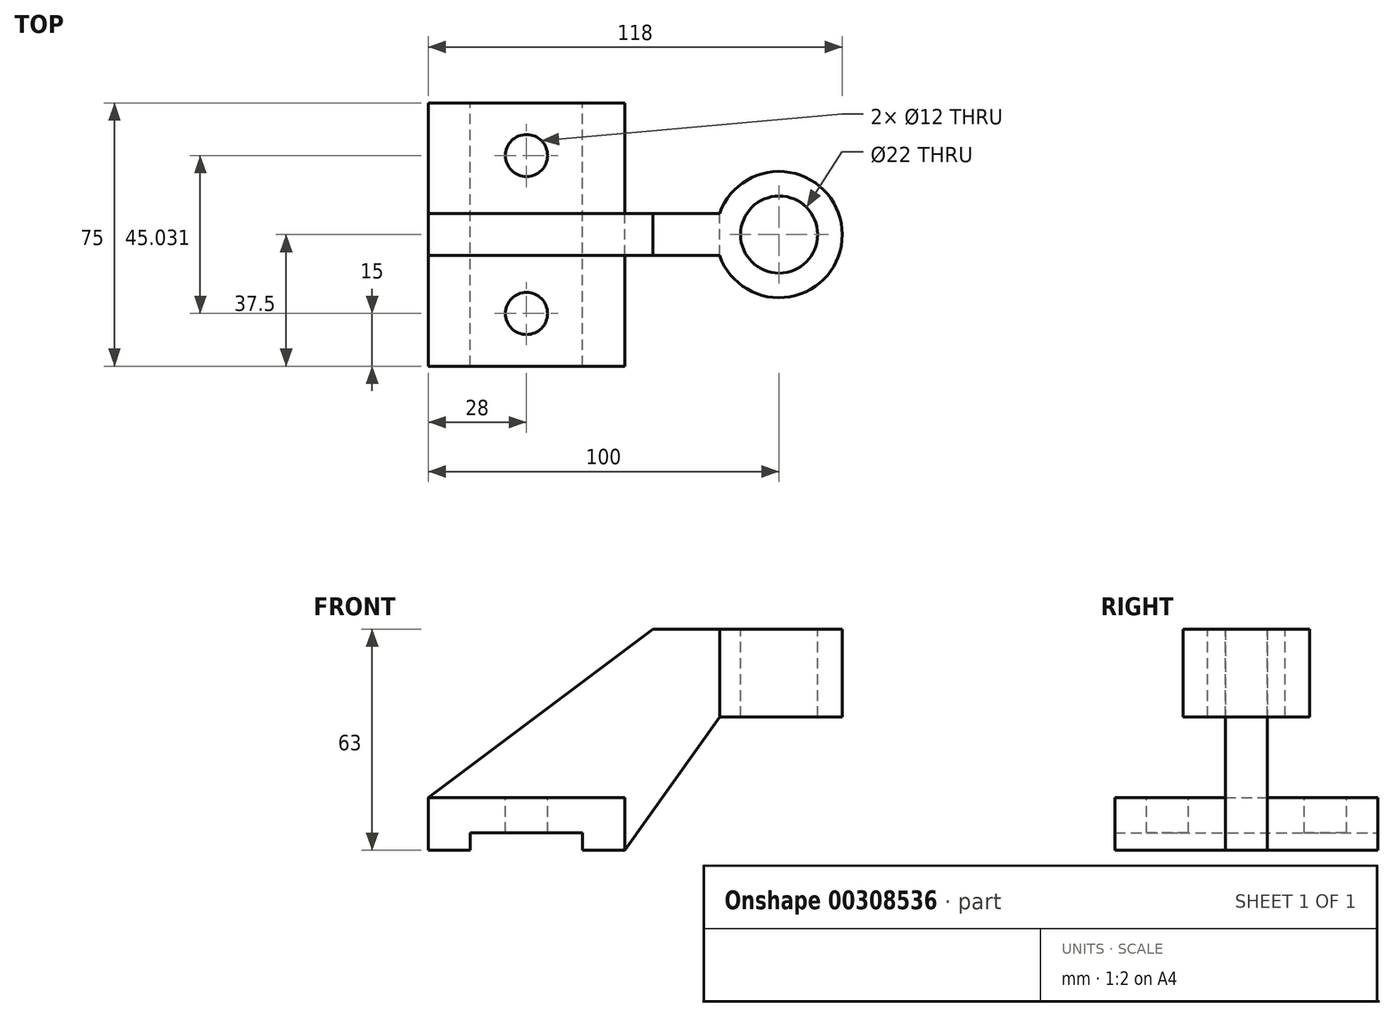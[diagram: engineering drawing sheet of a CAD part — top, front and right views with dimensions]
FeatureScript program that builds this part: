
annotation { "Feature Type Name" : "Feature", "Feature Type Description" : "" }
export const myFeature = defineFeature(function(context is Context, id is Id, definition is map)
    precondition{}
    {
        {
            var Q0;
            Q0=qCreatedBy(makeId("Front.planeOp"),FACE);
            var sketch = newSketch(context, id + "F0", { "sketchPlane" : qUnion([Q0])});
            skLineSegment(sketch, "E0", {"start": v(-0.42, 84.61) * mm, "end": v(99.58, 84.61) * mm, "construction": true});
            skPoint(sketch, "E1", {"position": v(0, 0) * mm});
            skLineSegment(sketch, "E2.bottom", {"start": v(0, 0) * mm, "end": v(56, 0) * mm});
            skLineSegment(sketch, "E2.top", {"start": v(0, 15) * mm, "end": v(56, 15) * mm});
            skLineSegment(sketch, "E2.left", {"start": v(0, 0) * mm, "end": v(0, 15) * mm});
            skLineSegment(sketch, "E2.right", {"start": v(56, 0) * mm, "end": v(56, 15) * mm});
            skLineSegment(sketch, "E3", {"start": v(12, 0) * mm, "end": v(12, 5) * mm});
            skLineSegment(sketch, "E4", {"start": v(12, 5) * mm, "end": v(44, 5) * mm});
            skLineSegment(sketch, "E5", {"start": v(44, 5) * mm, "end": v(44, 0) * mm});
            skLineSegment(sketch, "E6.bottom", {"start": v(82, 63) * mm, "end": v(118, 63) * mm});
            skLineSegment(sketch, "E6.top", {"start": v(82, 38) * mm, "end": v(118, 38) * mm});
            skLineSegment(sketch, "E6.left", {"start": v(82, 63) * mm, "end": v(82, 38) * mm, "construction": true});
            skLineSegment(sketch, "E6.right", {"start": v(118, 63) * mm, "end": v(118, 38) * mm});
            skLineSegment(sketch, "E7", {"start": v(82, 63) * mm, "end": v(64, 63) * mm});
            skLineSegment(sketch, "E8", {"start": v(64, 63) * mm, "end": v(0, 15) * mm});
            skLineSegment(sketch, "E9", {"start": v(100, 31) * mm, "end": v(100, 73.47) * mm, "construction": true});
            skCircle(sketch, "E10", {"center": v(100, 38) * mm, "radius": 18 * mm, "construction": true});
            skLineSegment(sketch, "E11", {"start": v(79.66, 32) * mm, "end": v(120.46, 32) * mm, "construction": true});
            skPoint(sketch, "E12", {"position": v(83.03, 32) * mm});
            skPoint(sketch, "E13", {"position": v(83.03, 38) * mm});
            skLineSegment(sketch, "E14", {"start": v(83.03, 38) * mm, "end": v(56, 0) * mm});
            skLineSegment(sketch, "E15", {"start": v(83.03, 38) * mm, "end": v(83.03, 63) * mm});
            skSolve(sketch);
        }
        {
            var Q0;
            Q0=makeQuery(id+"F0.imprint","IMPRINT",FACE,{"disambiguationData":[TD([[makeQuery(id+"F0.imprint","IMPRINT",EDGE,{"derivedFrom":sQuery(id+"F0.wireOp",EDGE,"E2.top")}),-1.0]])]});
            var Q1;
            {var subQ0=sQuery(id+"F0.wireOp",EDGE,"E6.right");Q1=makeQuery(id+"F0.imprint","IMPRINT",FACE,{"disambiguationData":[TD([[makeQuery(id+"F0.imprint","IMPRINT",EDGE,{"derivedFrom":subQ0}),-1.0]])]});}
            extrude(context, id + "F1", {"entities" : qUnion([Q0, Q1]), "endBound" : BoundingType.SYMMETRIC, "depth" : 75 * mm});
        }
        {
            var Q0;
            Q0=makeQuery(id+"F1.opExtrude","SWEPT_FACE",FACE,{"disambiguationData":[OSD([sQuery(id+"F0.wireOp",EDGE,"E6.bottom")])]});
            var sketch = newSketch(context, id + "F2", { "sketchPlane" : qUnion([Q0])});
            skPoint(sketch, "E16.0", {"position": v(100, 0) * mm});
            skCircle(sketch, "E17", {"center": v(100, 0) * mm, "radius": 11 * mm});
            skCircle(sketch, "E18", {"center": v(100, 0) * mm, "radius": 18 * mm});
            skLineSegment(sketch, "E19", {"start": v(-24.96, 0) * mm, "end": v(142.95, 0) * mm, "construction": true});
            skLineSegment(sketch, "E20.0", {"start": v(0, -37.5) * mm, "end": v(56, -37.5) * mm, "construction": true});
            skLineSegment(sketch, "E21", {"start": v(28, -46.15) * mm, "end": v(28, 43.3) * mm, "construction": true});
            skPoint(sketch, "E21.startSnap0", {"position": v(28, -37.5) * mm});
            skLineSegment(sketch, "E22", {"start": v(20.02, 22.53) * mm, "end": v(39.71, 22.53) * mm, "construction": true});
            skLineSegment(sketch, "E23", {"start": v(18.82, -22.5) * mm, "end": v(39.71, -22.5) * mm, "construction": true});
            skCircle(sketch, "E24", {"center": v(28, -22.5) * mm, "radius": 6 * mm});
            skCircle(sketch, "E25", {"center": v(28, 22.53) * mm, "radius": 6 * mm});
            skLineSegment(sketch, "E26.0", {"start": v(83.03, -37.5) * mm, "end": v(118, -37.5) * mm});
            skLineSegment(sketch, "E27.0", {"start": v(118, -37.5) * mm, "end": v(118, 37.5) * mm});
            skLineSegment(sketch, "E28.0", {"start": v(83.03, 37.5) * mm, "end": v(118, 37.5) * mm});
            skLineSegment(sketch, "E29.0", {"start": v(83.03, -37.5) * mm, "end": v(83.03, 37.5) * mm});
            skSolve(sketch);
        }
        {
            var Q0;
            Q0=makeQuery(id+"F2.imprint","IMPRINT",FACE,{"disambiguationData":[TD([[makeQuery(id+"F2.imprint","IMPRINT",EDGE,{"derivedFrom":sQuery(id+"F2.wireOp",EDGE,"E24")}),1.0]])]});
            var Q1;
            Q1=makeQuery(id+"F2.imprint","IMPRINT",FACE,{"disambiguationData":[TD([[makeQuery(id+"F2.imprint","IMPRINT",EDGE,{"derivedFrom":sQuery(id+"F2.wireOp",EDGE,"E17")}),1.0]])]});
            var Q2;
            Q2=makeQuery(id+"F2.imprint","IMPRINT",FACE,{"disambiguationData":[TD([[makeQuery(id+"F2.imprint","IMPRINT",EDGE,{"derivedFrom":sQuery(id+"F2.wireOp",EDGE,"E25")}),1.0]])]});
            var Q3;
            {var subQ5=sQuery(id+"F2.wireOp",EDGE,"E28.0");Q3=makeQuery(id+"F2.imprint","IMPRINT",FACE,{"disambiguationData":[TD([[makeQuery(id+"F2.imprint","IMPRINT",EDGE,{"derivedFrom":subQ5}),-1.0]])]});}
            var Q4;
            {var subQ5=sQuery(id+"F2.wireOp",EDGE,"E26.0");Q4=makeQuery(id+"F2.imprint","IMPRINT",FACE,{"disambiguationData":[TD([[makeQuery(id+"F2.imprint","IMPRINT",EDGE,{"derivedFrom":subQ5}),1.0]])]});}
            extrude(context, id + "F3", {"entities" : qUnion([Q0, Q1, Q2, Q3, Q4]), "operationType" : NewBodyOperationType.REMOVE, "endBound" : BoundingType.THROUGH_ALL, "oppositeDirection" : true, "depth" : 25 * mm});
        }
        {
            var Q0;
            Q0=makeQuery(id+"F0.imprint","IMPRINT",FACE,{"disambiguationData":[TD([[makeQuery(id+"F0.imprint","IMPRINT",EDGE,{"derivedFrom":sQuery(id+"F0.wireOp",EDGE,"E2.top")}),1.0]])]});
            extrude(context, id + "F4", {"entities" : qUnion([Q0]), "operationType" : NewBodyOperationType.ADD, "endBound" : BoundingType.SYMMETRIC, "depth" : 12 * mm});
        }
    });
